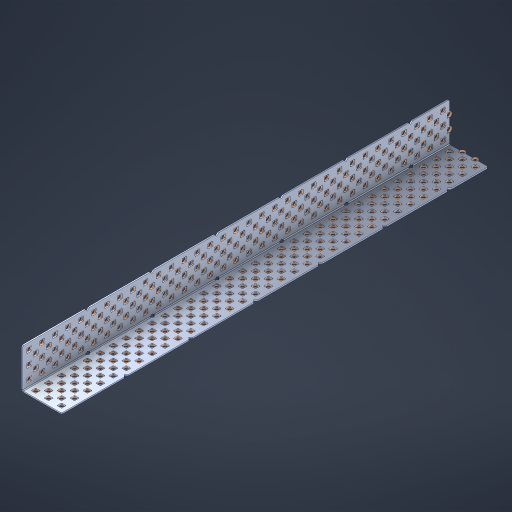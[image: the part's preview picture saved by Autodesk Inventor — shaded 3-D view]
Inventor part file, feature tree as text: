
AUTODESK INVENTOR PART (.ipt)
format: ipt  version: 2023 (Build 270158000, 158)  size: 3,256,320 bytes
history: native  units: in
note: dims shown in document units (in); Inventor stores cm internally (conversion verified against a paired STEP export)
features: other x336, extrude x328, sheet_metal_op x8, sketch x7, pattern_linear x3, mirror x1, chamfer x1
ambient origin geometry x8: Origin, YZ Plane, XZ Plane, XY Plane, X Axis, Y Axis, Z Axis, Center Point
bodies: Solid1 (feature_tree), Body (feature_tree)
feature tree (684):
  sheet_metal_op  "Flanges"
  sheet_metal_op  "Body Pattern"
  pattern_linear  "Center Double"  Spacing1=1.5in  [1 undecoded]
  pattern_linear  "Center Pattern"  Spacing1=0.1875in  [1 undecoded]
  other  "Arc Length"
  pattern_linear  "Notch Pattern"  Spacing1=0.0469in  [1 undecoded]
  other  "Diagonal Plane"
  mirror  "Everything Mirrored"
  chamfer  "End Chamfer"
  sketch  "Sketch1"  dims[d0=1.5in]
  other  "Plate1"
  sketch  "Sketch2"  dims[d1=16.5in]
  other  "Plate2"
  sheet_metal_op  "Bend1"
  sheet_metal_op  "Corner1"
  sketch  "Sketch8"  dims[d2=0.0469in]
  sketch  "Sketch9"  dims[d3=0.0469in]
  other  "Srf91"
  sheet_metal_op  "Body Pattern Sketch"
  other  "Srf92"
  sketch  "Sketch13"  dims[d4=0.0234in]
  sketch  "Sketch15"  dims[d5=0.0938in]
  sketch  "Sketch16"  dims[d6=0.0469in d7=1.5in d8=90.0deg d9=0.0312in d10=0.1875in d11=0.0469in d12=0.0469in d49=0.182in d50=0.02in d52=0.25in d53=0.0469in d54=0.0in d55=0.172in d56=1.0in d57=0.0in d85=0.1473in d86=0.1659in d89=0.0469in d90=0.0in d91=0.04in d92=0.0491in d95=2.5in d96=0.04in d97=0.25in d98=45.0deg d106=0.182in d107=0.02in d110=0.0469in d111=0.0in d112=0.172in d113=0.5in d114=0.0in d117=0.5in d126=0.0491in d127=0.1227in d128=0.08in d129=0.04in d130=2.5in d131=0.25in d132=12.9921in d134=0.5in d135=1.1811in d137=0.5in d140=0.5in d141=1.0in d142=0.3937in d144=0.5in d145=0.071in d146=0.7874in d148=0.5in]
  other  "Srf786"
  other  "Srf856"
  other  "Srf889"
  other  "Srf890"
  other  "Srf891"
  other  "Srf1275"
  other  "Srf1276"
  other  "Srf1278"
  other  "Srf1277"
  other  "Srf1285"
  other  "Srf1286"
  other  "Srf1287"
  other  "Srf1445"
  other  "Srf1446"
  other  "Srf1447"
  other  "Srf1448"
  other  "Srf1449"
  other  "Srf1537"
  other  "Srf1538"
  other  "Srf1539"
  other  "Srf1540"
  other  "Srf1541"
  other  "Srf1807"
  other  "Srf1808"
  other  "Srf1809"
  other  "Srf1810"
  other  "Srf1811"
  other  "Srf1812"
  other  "Srf1813"
  other  "Srf1814"
  other  "Srf1815"
  other  "Srf1816"
  other  "Srf1817"
  other  "Srf1818"
  other  "Srf1819"
  other  "Srf1820"
  other  "Srf1821"
  other  "Srf1822"
  other  "Srf1823"
  other  "Srf1824"
  other  "Srf1825"
  other  "Srf1826"
  other  "Srf1827"
  other  "Srf1828"
  other  "Srf1829"
  other  "Srf1830"
  other  "Srf1959"
  other  "Srf1960"
  other  "Srf1961"
  other  "Srf1962"
  other  "Srf1963"
  other  "Srf1964"
  other  "Srf1965"
  other  "Srf1966"
  other  "Srf1967"
  other  "Srf1968"
  other  "Srf1969"
  other  "Srf1970"
  other  "Srf1971"
  other  "Srf1972"
  other  "Srf1973"
  other  "Srf1974"
  other  "Srf1975"
  other  "Srf1976"
  other  "Srf1977"
  other  "Srf1978"
  other  "Srf1979"
  other  "Srf1980"
  other  "Srf1981"
  other  "Srf1982"
  other  "Srf2009"
  other  "Srf2010"
  other  "Srf2011"
  other  "Srf2012"
  other  "Srf2013"
  other  "Srf2014"
  other  "Srf2015"
  other  "Srf2016"
  other  "Srf2017"
  other  "Srf2018"
  other  "Srf2019"
  other  "Srf2020"
  other  "Srf2021"
  other  "Srf2022"
  other  "Srf2023"
  other  "Srf2024"
  other  "Srf2025"
  other  "Srf2026"
  other  "Srf2027"
  other  "Srf2028"
  other  "Srf2029"
  other  "Srf2030"
  other  "Srf2031"
  other  "Srf2032"
  other  "Srf2033"
  other  "Srf2034"
  other  "Srf2035"
  other  "Srf2036"
  other  "Srf2037"
  other  "Srf2038"
  other  "Srf2039"
  other  "Srf2040"
  other  "Srf2041"
  other  "Srf2043"
  other  "Srf2044"
  other  "Srf2045"
  other  "Srf2046"
  other  "Srf2047"
  other  "Srf2048"
  other  "Srf2049"
  other  "Srf2050"
  other  "Srf2051"
  other  "Srf2052"
  other  "Srf2053"
  other  "Srf2054"
  other  "Srf2055"
  other  "Srf2056"
  other  "Srf2057"
  other  "Srf2058"
  other  "Srf2059"
  other  "Srf2060"
  other  "Srf2061"
  other  "Srf2062"
  other  "Srf2063"
  other  "Srf2064"
  other  "Srf2065"
  other  "Srf2066"
  other  "Srf2067"
  other  "Srf2068"
  other  "Srf2069"
  other  "Srf2070"
  other  "Srf2071"
  other  "Srf2072"
  other  "Srf2073"
  other  "Srf2074"
  other  "Srf2076"
  other  "Srf2077"
  other  "Srf2078"
  other  "Srf2079"
  other  "Srf2080"
  other  "Srf2081"
  other  "Srf2082"
  other  "Srf2083"
  other  "Srf2084"
  other  "Srf2085"
  other  "Srf2086"
  other  "Srf2087"
  other  "Srf2088"
  other  "Srf2089"
  other  "Srf2090"
  other  "Srf2091"
  other  "Srf2092"
  other  "Srf2093"
  other  "Srf2094"
  other  "Srf2095"
  other  "Srf2096"
  other  "Srf2097"
  other  "Srf2098"
  other  "Srf2099"
  other  "Srf2100"
  other  "Srf2101"
  other  "Srf2102"
  other  "Srf2103"
  other  "Srf2104"
  other  "Srf2105"
  other  "Srf2106"
  other  "Srf2107"
  other  "Srf2108"
  other  "Srf2109"
  other  "Srf2110"
  other  "Srf2111"
  other  "Srf2112"
  other  "Srf2113"
  other  "Srf2114"
  other  "Srf2115"
  other  "Srf2116"
  other  "Srf2117"
  other  "Srf2118"
  other  "Srf2119"
  other  "Srf2120"
  other  "Srf2121"
  other  "Srf2122"
  other  "Srf2123"
  other  "Srf2124"
  other  "Srf2125"
  other  "Srf2126"
  other  "Srf2127"
  other  "Srf2128"
  other  "Srf2129"
  other  "Srf2130"
  other  "Srf2131"
  other  "Srf2132"
  other  "Srf2133"
  other  "Srf2134"
  other  "Srf2135"
  other  "Srf2136"
  other  "Srf2137"
  other  "Srf2138"
  other  "Srf2139"
  other  "Srf2140"
  other  "Srf2141"
  other  "Srf2142"
  other  "Srf2143"
  other  "Srf2144"
  other  "Srf2145"
  other  "Srf2146"
  other  "Srf2147"
  other  "Srf2148"
  other  "Srf2149"
  other  "Srf2150"
  other  "Srf2151"
  other  "Srf2152"
  other  "Srf2153"
  other  "Srf2154"
  other  "Srf2155"
  other  "Srf2156"
  other  "Srf2157"
  other  "Srf2158"
  other  "Srf2159"
  other  "Srf2160"
  other  "Srf2161"
  other  "Srf2162"
  other  "Srf2163"
  other  "Srf2164"
  other  "Srf2165"
  other  "Srf2166"
  other  "Srf2167"
  other  "Srf2168"
  other  "Srf2169"
  other  "Srf2170"
  other  "Srf2171"
  other  "Srf2172"
  other  "Srf2179"
  other  "Srf2180"
  other  "Srf2181"
  other  "Srf2182"
  other  "Srf2183"
  other  "Srf2184"
  other  "Srf2185"
  other  "Srf2186"
  other  "Srf2187"
  other  "Srf2188"
  other  "Srf2189"
  other  "Srf2190"
  other  "Srf2191"
  other  "Srf2192"
  other  "Srf2193"
  other  "Srf2194"
  other  "Srf2195"
  other  "Srf2196"
  other  "Srf2197"
  other  "Srf2198"
  other  "Srf2199"
  other  "Srf2200"
  other  "Srf2201"
  other  "Srf2202"
  other  "Srf2203"
  other  "Srf2204"
  other  "Srf2205"
  other  "Srf2206"
  other  "Srf2207"
  other  "Srf2208"
  other  "Srf2209"
  other  "Srf2210"
  other  "Srf2211"
  other  "Srf2212"
  other  "Srf2213"
  other  "Srf2214"
  other  "Srf2215"
  other  "Srf2216"
  other  "Srf2217"
  other  "Srf2218"
  other  "Srf2219"
  other  "Srf2220"
  other  "Srf2221"
  other  "Srf2222"
  other  "Srf2223"
  other  "Srf2224"
  other  "Srf2225"
  other  "Srf2226"
  other  "Srf2227"
  other  "Srf2228"
  other  "Srf2229"
  other  "Srf2230"
  other  "Srf2231"
  other  "Srf2232"
  other  "Srf2233"
  other  "Srf2234"
  other  "Srf2235"
  other  "Srf2236"
  other  "Srf2237"
  other  "Srf2238"
  other  "Srf2239"
  other  "Srf2240"
  other  "Srf2241"
  other  "Srf2242"
  other  "Srf2243"
  other  "Srf2244"
  other  "Srf2245"
  other  "Srf2246"
  other  "Srf2247"
  other  "Srf2248"
  other  "Srf2249"
  other  "Srf2250"
  other  "Srf2251"
  other  "Srf2252"
  other  "Srf2253"
  other  "Srf2254"
  other  "Srf2255"
  other  "Srf2256"
  other  "Srf2257"
  other  "Srf2258"
  other  "Srf2259"
  other  "Srf2260"
  other  "Srf2261"
  other  "Srf2262"
  other  "Srf2263"
  other  "Srf2264"
  other  "Srf2265"
  other  "Srf2266"
  other  "Srf2267"
  other  "Srf2268"
  other  "Srf2269"
  other  "Srf2270"
  other  "Srf2271"
  other  "Srf2272"
  other  "Srf2273"
  other  "Srf2274"
  sheet_metal_op  "Body Stamp"
  sheet_metal_op  "Body Circle"
  other  "Center Stamp"
  other  "Center Circle"
  sheet_metal_op  "Notch"
  extrude  "ExtrusionSrf92"  Depth=0.0469in
  extrude  "ExtrusionSrf856"  Depth=0.182in
  extrude  "ExtrusionSrf889"  Depth=0.02in
  extrude  "ExtrusionSrf890"  Depth=0.25in
  extrude  "ExtrusionSrf891"  Depth=0.0469in
  extrude  "ExtrusionSrf1275"  TaperAngle=0.0deg  [1 undecoded]
  extrude  "ExtrusionSrf1276"  Depth=0.5in
  extrude  "ExtrusionSrf1277"  Depth=1.0in TaperAngle=0.0deg
  extrude  "ExtrusionSrf1345"  Depth=0.5in
  extrude  "ExtrusionSrf1346"  Depth=0.5in
  extrude  "ExtrusionSrf1347"  Depth=0.0469in
  extrude  "ExtrusionSrf1348"  Depth=0.5in TaperAngle=0.0deg
  extrude  "ExtrusionSrf1445"  Depth=0.5in
  extrude  "ExtrusionSrf1446"  Depth=0.25in TaperAngle=45.0deg
  extrude  "ExtrusionSrf1447"  Depth=0.182in
  extrude  "ExtrusionSrf1448"  Depth=0.02in
  extrude  "ExtrusionSrf1449"  Depth=0.0469in
  extrude  "ExtrusionSrf1537"  TaperAngle=0.0deg  [1 undecoded]
  extrude  "ExtrusionSrf1538"  Depth=0.5in
  extrude  "ExtrusionSrf1539"  Depth=0.5in TaperAngle=0.0deg
  extrude  "ExtrusionSrf1540"  Depth=0.5in
  extrude  "ExtrusionSrf1541"  Depth=0.5in
  extrude  "ExtrusionSrf1807"  Depth=0.5in
  extrude  "ExtrusionSrf1808"  Depth=0.5in
  extrude  "ExtrusionSrf1809"  Depth=0.5in
  extrude  "ExtrusionSrf1810"  Depth=0.5in
  extrude  "ExtrusionSrf1811"  Depth=0.25in
  extrude  "ExtrusionSrf1812"  Depth=0.5in
  extrude  "ExtrusionSrf1813"  Depth=0.5in
  extrude  "ExtrusionSrf1814"  Depth=0.5in
  extrude  "ExtrusionSrf1815"  Depth=1.0in
  extrude  "ExtrusionSrf1816"  Depth=0.3937in
  extrude  "ExtrusionSrf1817"  Depth=0.5in
  extrude  "ExtrusionSrf1818"  Depth=0.5in
  extrude  "ExtrusionSrf1819"  [1 undecoded]
  extrude  "ExtrusionSrf1820"  [1 undecoded]
  extrude  "ExtrusionSrf1821"  [1 undecoded]
  extrude  "ExtrusionSrf1822"  [1 undecoded]
  extrude  "ExtrusionSrf1823"  [1 undecoded]
  extrude  "ExtrusionSrf1824"  [1 undecoded]
  extrude  "ExtrusionSrf1825"  [1 undecoded]
  extrude  "ExtrusionSrf1826"  [1 undecoded]
  extrude  "ExtrusionSrf1827"  [1 undecoded]
  extrude  "ExtrusionSrf1828"  [1 undecoded]
  extrude  "ExtrusionSrf1829"  [1 undecoded]
  extrude  "ExtrusionSrf1830"  [1 undecoded]
  extrude  "ExtrusionSrf1959"  [1 undecoded]
  extrude  "ExtrusionSrf1960"  [1 undecoded]
  extrude  "ExtrusionSrf1961"  [1 undecoded]
  extrude  "ExtrusionSrf1962"  [1 undecoded]
  extrude  "ExtrusionSrf1963"  [1 undecoded]
  extrude  "ExtrusionSrf1964"  [1 undecoded]
  extrude  "ExtrusionSrf1965"  [1 undecoded]
  extrude  "ExtrusionSrf1966"  [1 undecoded]
  extrude  "ExtrusionSrf1967"  [1 undecoded]
  extrude  "ExtrusionSrf1968"  [1 undecoded]
  extrude  "ExtrusionSrf1969"  [1 undecoded]
  extrude  "ExtrusionSrf1970"  [1 undecoded]
  extrude  "ExtrusionSrf1971"  [1 undecoded]
  extrude  "ExtrusionSrf1972"  [1 undecoded]
  extrude  "ExtrusionSrf1973"  [1 undecoded]
  extrude  "ExtrusionSrf1974"  [1 undecoded]
  extrude  "ExtrusionSrf1975"  [1 undecoded]
  extrude  "ExtrusionSrf1976"  [1 undecoded]
  extrude  "ExtrusionSrf1977"  [1 undecoded]
  extrude  "ExtrusionSrf1978"  [1 undecoded]
  extrude  "ExtrusionSrf1979"  [1 undecoded]
  extrude  "ExtrusionSrf1980"  [1 undecoded]
  extrude  "ExtrusionSrf1981"  [1 undecoded]
  extrude  "ExtrusionSrf1982"  [1 undecoded]
  extrude  "ExtrusionSrf2009"  [1 undecoded]
  extrude  "ExtrusionSrf2010"  [1 undecoded]
  extrude  "ExtrusionSrf2011"  [1 undecoded]
  extrude  "ExtrusionSrf2012"  [1 undecoded]
  extrude  "ExtrusionSrf2013"  [1 undecoded]
  extrude  "ExtrusionSrf2014"  [1 undecoded]
  extrude  "ExtrusionSrf2015"  [1 undecoded]
  extrude  "ExtrusionSrf2016"  [1 undecoded]
  extrude  "ExtrusionSrf2017"  [1 undecoded]
  extrude  "ExtrusionSrf2018"  [1 undecoded]
  extrude  "ExtrusionSrf2019"  [1 undecoded]
  extrude  "ExtrusionSrf2020"  [1 undecoded]
  extrude  "ExtrusionSrf2021"  [1 undecoded]
  extrude  "ExtrusionSrf2022"  [1 undecoded]
  extrude  "ExtrusionSrf2023"  [1 undecoded]
  extrude  "ExtrusionSrf2024"  [1 undecoded]
  extrude  "ExtrusionSrf2025"  [1 undecoded]
  extrude  "ExtrusionSrf2026"  [1 undecoded]
  extrude  "ExtrusionSrf2027"  [1 undecoded]
  extrude  "ExtrusionSrf2028"  [1 undecoded]
  extrude  "ExtrusionSrf2029"  [1 undecoded]
  extrude  "ExtrusionSrf2030"  [1 undecoded]
  extrude  "ExtrusionSrf2031"  [1 undecoded]
  extrude  "ExtrusionSrf2032"  [1 undecoded]
  extrude  "ExtrusionSrf2033"  [1 undecoded]
  extrude  "ExtrusionSrf2034"  [1 undecoded]
  extrude  "ExtrusionSrf2035"  [1 undecoded]
  extrude  "ExtrusionSrf2036"  [1 undecoded]
  extrude  "ExtrusionSrf2037"  [1 undecoded]
  extrude  "ExtrusionSrf2038"  [1 undecoded]
  extrude  "ExtrusionSrf2039"  [1 undecoded]
  extrude  "ExtrusionSrf2040"  [1 undecoded]
  extrude  "ExtrusionSrf2041"  [1 undecoded]
  extrude  "ExtrusionSrf2043"  [1 undecoded]
  extrude  "ExtrusionSrf2044"  [1 undecoded]
  extrude  "ExtrusionSrf2045"  [1 undecoded]
  extrude  "ExtrusionSrf2046"  [1 undecoded]
  extrude  "ExtrusionSrf2047"  [1 undecoded]
  extrude  "ExtrusionSrf2048"  [1 undecoded]
  extrude  "ExtrusionSrf2049"  [1 undecoded]
  extrude  "ExtrusionSrf2050"  [1 undecoded]
  extrude  "ExtrusionSrf2051"  [1 undecoded]
  extrude  "ExtrusionSrf2052"  [1 undecoded]
  extrude  "ExtrusionSrf2053"  [1 undecoded]
  extrude  "ExtrusionSrf2054"  [1 undecoded]
  extrude  "ExtrusionSrf2055"  [1 undecoded]
  extrude  "ExtrusionSrf2056"  [1 undecoded]
  extrude  "ExtrusionSrf2057"  [1 undecoded]
  extrude  "ExtrusionSrf2058"  [1 undecoded]
  extrude  "ExtrusionSrf2059"  [1 undecoded]
  extrude  "ExtrusionSrf2060"  [1 undecoded]
  extrude  "ExtrusionSrf2061"  [1 undecoded]
  extrude  "ExtrusionSrf2062"  [1 undecoded]
  extrude  "ExtrusionSrf2063"  [1 undecoded]
  extrude  "ExtrusionSrf2064"  [1 undecoded]
  extrude  "ExtrusionSrf2065"  [1 undecoded]
  extrude  "ExtrusionSrf2066"  [1 undecoded]
  extrude  "ExtrusionSrf2067"  [1 undecoded]
  extrude  "ExtrusionSrf2068"  [1 undecoded]
  extrude  "ExtrusionSrf2069"  [1 undecoded]
  extrude  "ExtrusionSrf2070"  [1 undecoded]
  extrude  "ExtrusionSrf2071"  [1 undecoded]
  extrude  "ExtrusionSrf2072"  [1 undecoded]
  extrude  "ExtrusionSrf2073"  [1 undecoded]
  extrude  "ExtrusionSrf2074"  [1 undecoded]
  extrude  "ExtrusionSrf2076"  [1 undecoded]
  extrude  "ExtrusionSrf2077"  [1 undecoded]
  extrude  "ExtrusionSrf2078"  [1 undecoded]
  extrude  "ExtrusionSrf2079"  [1 undecoded]
  extrude  "ExtrusionSrf2080"  [1 undecoded]
  extrude  "ExtrusionSrf2081"  [1 undecoded]
  extrude  "ExtrusionSrf2082"  [1 undecoded]
  extrude  "ExtrusionSrf2083"  [1 undecoded]
  extrude  "ExtrusionSrf2084"  [1 undecoded]
  extrude  "ExtrusionSrf2085"  [1 undecoded]
  extrude  "ExtrusionSrf2086"  [1 undecoded]
  extrude  "ExtrusionSrf2087"  [1 undecoded]
  extrude  "ExtrusionSrf2088"  [1 undecoded]
  extrude  "ExtrusionSrf2089"  [1 undecoded]
  extrude  "ExtrusionSrf2090"  [1 undecoded]
  extrude  "ExtrusionSrf2091"  [1 undecoded]
  extrude  "ExtrusionSrf2092"  [1 undecoded]
  extrude  "ExtrusionSrf2093"  [1 undecoded]
  extrude  "ExtrusionSrf2094"  [1 undecoded]
  extrude  "ExtrusionSrf2095"  [1 undecoded]
  extrude  "ExtrusionSrf2096"  [1 undecoded]
  extrude  "ExtrusionSrf2097"  [1 undecoded]
  extrude  "ExtrusionSrf2098"  [1 undecoded]
  extrude  "ExtrusionSrf2099"  [1 undecoded]
  extrude  "ExtrusionSrf2100"  [1 undecoded]
  extrude  "ExtrusionSrf2101"  [1 undecoded]
  extrude  "ExtrusionSrf2102"  [1 undecoded]
  extrude  "ExtrusionSrf2103"  [1 undecoded]
  extrude  "ExtrusionSrf2104"  [1 undecoded]
  extrude  "ExtrusionSrf2105"  [1 undecoded]
  extrude  "ExtrusionSrf2106"  [1 undecoded]
  extrude  "ExtrusionSrf2107"  [1 undecoded]
  extrude  "ExtrusionSrf2108"  [1 undecoded]
  extrude  "ExtrusionSrf2109"  [1 undecoded]
  extrude  "ExtrusionSrf2110"  [1 undecoded]
  extrude  "ExtrusionSrf2111"  [1 undecoded]
  extrude  "ExtrusionSrf2112"  [1 undecoded]
  extrude  "ExtrusionSrf2113"  [1 undecoded]
  extrude  "ExtrusionSrf2114"  [1 undecoded]
  extrude  "ExtrusionSrf2115"  [1 undecoded]
  extrude  "ExtrusionSrf2116"  [1 undecoded]
  extrude  "ExtrusionSrf2117"  [1 undecoded]
  extrude  "ExtrusionSrf2118"  [1 undecoded]
  extrude  "ExtrusionSrf2119"  [1 undecoded]
  extrude  "ExtrusionSrf2120"  [1 undecoded]
  extrude  "ExtrusionSrf2121"  [1 undecoded]
  extrude  "ExtrusionSrf2122"  [1 undecoded]
  extrude  "ExtrusionSrf2123"  [1 undecoded]
  extrude  "ExtrusionSrf2124"  [1 undecoded]
  extrude  "ExtrusionSrf2125"  [1 undecoded]
  extrude  "ExtrusionSrf2126"  [1 undecoded]
  extrude  "ExtrusionSrf2127"  [1 undecoded]
  extrude  "ExtrusionSrf2128"  [1 undecoded]
  extrude  "ExtrusionSrf2129"  [1 undecoded]
  extrude  "ExtrusionSrf2130"  [1 undecoded]
  extrude  "ExtrusionSrf2131"  [1 undecoded]
  extrude  "ExtrusionSrf2132"  [1 undecoded]
  extrude  "ExtrusionSrf2133"  [1 undecoded]
  extrude  "ExtrusionSrf2134"  [1 undecoded]
  extrude  "ExtrusionSrf2135"  [1 undecoded]
  extrude  "ExtrusionSrf2136"  [1 undecoded]
  extrude  "ExtrusionSrf2137"  [1 undecoded]
  extrude  "ExtrusionSrf2138"  [1 undecoded]
  extrude  "ExtrusionSrf2139"  [1 undecoded]
  extrude  "ExtrusionSrf2140"  [1 undecoded]
  extrude  "ExtrusionSrf2141"  [1 undecoded]
  extrude  "ExtrusionSrf2142"  [1 undecoded]
  extrude  "ExtrusionSrf2143"  [1 undecoded]
  extrude  "ExtrusionSrf2144"  [1 undecoded]
  extrude  "ExtrusionSrf2145"  [1 undecoded]
  extrude  "ExtrusionSrf2146"  [1 undecoded]
  extrude  "ExtrusionSrf2147"  [1 undecoded]
  extrude  "ExtrusionSrf2148"  [1 undecoded]
  extrude  "ExtrusionSrf2149"  [1 undecoded]
  extrude  "ExtrusionSrf2150"  [1 undecoded]
  extrude  "ExtrusionSrf2151"  [1 undecoded]
  extrude  "ExtrusionSrf2152"  [1 undecoded]
  extrude  "ExtrusionSrf2153"  [1 undecoded]
  extrude  "ExtrusionSrf2154"  [1 undecoded]
  extrude  "ExtrusionSrf2155"  [1 undecoded]
  extrude  "ExtrusionSrf2156"  [1 undecoded]
  extrude  "ExtrusionSrf2157"  [1 undecoded]
  extrude  "ExtrusionSrf2158"  [1 undecoded]
  extrude  "ExtrusionSrf2159"  [1 undecoded]
  extrude  "ExtrusionSrf2160"  [1 undecoded]
  extrude  "ExtrusionSrf2161"  [1 undecoded]
  extrude  "ExtrusionSrf2162"  [1 undecoded]
  extrude  "ExtrusionSrf2163"  [1 undecoded]
  extrude  "ExtrusionSrf2164"  [1 undecoded]
  extrude  "ExtrusionSrf2165"  [1 undecoded]
  extrude  "ExtrusionSrf2166"  [1 undecoded]
  extrude  "ExtrusionSrf2167"  [1 undecoded]
  extrude  "ExtrusionSrf2168"  [1 undecoded]
  extrude  "ExtrusionSrf2169"  [1 undecoded]
  extrude  "ExtrusionSrf2170"  [1 undecoded]
  extrude  "ExtrusionSrf2171"  [1 undecoded]
  extrude  "ExtrusionSrf2172"  [1 undecoded]
  extrude  "ExtrusionSrf2179"  [1 undecoded]
  extrude  "ExtrusionSrf2180"  [1 undecoded]
  extrude  "ExtrusionSrf2181"  [1 undecoded]
  extrude  "ExtrusionSrf2182"  [1 undecoded]
  extrude  "ExtrusionSrf2183"  [1 undecoded]
  extrude  "ExtrusionSrf2184"  [1 undecoded]
  extrude  "ExtrusionSrf2185"  [1 undecoded]
  extrude  "ExtrusionSrf2186"  [1 undecoded]
  extrude  "ExtrusionSrf2187"  [1 undecoded]
  extrude  "ExtrusionSrf2188"  [1 undecoded]
  extrude  "ExtrusionSrf2189"  [1 undecoded]
  extrude  "ExtrusionSrf2190"  [1 undecoded]
  extrude  "ExtrusionSrf2191"  [1 undecoded]
  extrude  "ExtrusionSrf2192"  [1 undecoded]
  extrude  "ExtrusionSrf2193"  [1 undecoded]
  extrude  "ExtrusionSrf2194"  [1 undecoded]
  extrude  "ExtrusionSrf2195"  [1 undecoded]
  extrude  "ExtrusionSrf2196"  [1 undecoded]
  extrude  "ExtrusionSrf2197"  [1 undecoded]
  extrude  "ExtrusionSrf2198"  [1 undecoded]
  extrude  "ExtrusionSrf2199"  [1 undecoded]
  extrude  "ExtrusionSrf2200"  [1 undecoded]
  extrude  "ExtrusionSrf2201"  [1 undecoded]
  extrude  "ExtrusionSrf2202"  [1 undecoded]
  extrude  "ExtrusionSrf2203"  [1 undecoded]
  extrude  "ExtrusionSrf2204"  [1 undecoded]
  extrude  "ExtrusionSrf2205"  [1 undecoded]
  extrude  "ExtrusionSrf2206"  [1 undecoded]
  extrude  "ExtrusionSrf2207"  [1 undecoded]
  extrude  "ExtrusionSrf2208"  [1 undecoded]
  extrude  "ExtrusionSrf2209"  [1 undecoded]
  extrude  "ExtrusionSrf2210"  [1 undecoded]
  extrude  "ExtrusionSrf2211"  [1 undecoded]
  extrude  "ExtrusionSrf2212"  [1 undecoded]
  extrude  "ExtrusionSrf2213"  [1 undecoded]
  extrude  "ExtrusionSrf2214"  [1 undecoded]
  extrude  "ExtrusionSrf2215"  [1 undecoded]
  extrude  "ExtrusionSrf2216"  [1 undecoded]
  extrude  "ExtrusionSrf2217"  [1 undecoded]
  extrude  "ExtrusionSrf2218"  [1 undecoded]
  extrude  "ExtrusionSrf2219"  [1 undecoded]
  extrude  "ExtrusionSrf2220"  [1 undecoded]
  extrude  "ExtrusionSrf2221"  [1 undecoded]
  extrude  "ExtrusionSrf2222"  [1 undecoded]
  extrude  "ExtrusionSrf2223"  [1 undecoded]
  extrude  "ExtrusionSrf2224"  [1 undecoded]
  extrude  "ExtrusionSrf2225"  [1 undecoded]
  extrude  "ExtrusionSrf2226"  [1 undecoded]
  extrude  "ExtrusionSrf2227"  [1 undecoded]
  extrude  "ExtrusionSrf2228"  [1 undecoded]
  extrude  "ExtrusionSrf2229"  [1 undecoded]
  extrude  "ExtrusionSrf2230"  [1 undecoded]
  extrude  "ExtrusionSrf2231"  [1 undecoded]
  extrude  "ExtrusionSrf2232"  [1 undecoded]
  extrude  "ExtrusionSrf2233"  [1 undecoded]
  extrude  "ExtrusionSrf2234"  [1 undecoded]
  extrude  "ExtrusionSrf2235"  [1 undecoded]
  extrude  "ExtrusionSrf2236"  [1 undecoded]
  extrude  "ExtrusionSrf2237"  [1 undecoded]
  extrude  "ExtrusionSrf2238"  [1 undecoded]
  extrude  "ExtrusionSrf2239"  [1 undecoded]
  extrude  "ExtrusionSrf2240"  [1 undecoded]
  extrude  "ExtrusionSrf2241"  [1 undecoded]
  extrude  "ExtrusionSrf2242"  [1 undecoded]
  extrude  "ExtrusionSrf2243"  [1 undecoded]
  extrude  "ExtrusionSrf2244"  [1 undecoded]
  extrude  "ExtrusionSrf2245"  [1 undecoded]
  extrude  "ExtrusionSrf2246"  [1 undecoded]
  extrude  "ExtrusionSrf2247"  [1 undecoded]
  extrude  "ExtrusionSrf2248"  [1 undecoded]
  extrude  "ExtrusionSrf2249"  [1 undecoded]
  extrude  "ExtrusionSrf2250"  [1 undecoded]
  extrude  "ExtrusionSrf2251"  [1 undecoded]
  extrude  "ExtrusionSrf2252"  [1 undecoded]
  extrude  "ExtrusionSrf2253"  [1 undecoded]
  extrude  "ExtrusionSrf2254"  [1 undecoded]
  extrude  "ExtrusionSrf2255"  [1 undecoded]
  extrude  "ExtrusionSrf2256"  [1 undecoded]
  extrude  "ExtrusionSrf2257"  [1 undecoded]
  extrude  "ExtrusionSrf2258"  [1 undecoded]
  extrude  "ExtrusionSrf2259"  [1 undecoded]
  extrude  "ExtrusionSrf2260"  [1 undecoded]
  extrude  "ExtrusionSrf2261"  [1 undecoded]
  extrude  "ExtrusionSrf2262"  [1 undecoded]
  extrude  "ExtrusionSrf2263"  [1 undecoded]
  extrude  "ExtrusionSrf2264"  [1 undecoded]
  extrude  "ExtrusionSrf2265"  [1 undecoded]
  extrude  "ExtrusionSrf2266"  [1 undecoded]
  extrude  "ExtrusionSrf2267"  [1 undecoded]
  extrude  "ExtrusionSrf2268"  [1 undecoded]
  extrude  "ExtrusionSrf2269"  [1 undecoded]
  extrude  "ExtrusionSrf2270"  [1 undecoded]
  extrude  "ExtrusionSrf2271"  [1 undecoded]
  extrude  "ExtrusionSrf2272"  [1 undecoded]
  extrude  "ExtrusionSrf2273"  [1 undecoded]
  extrude  "ExtrusionSrf2274"  [1 undecoded]
note: 299 required parameter values undecoded (feature->parameter linkage not recoverable at this tier; creation-order binding heuristic only, values carry confidence <= 0.55)
